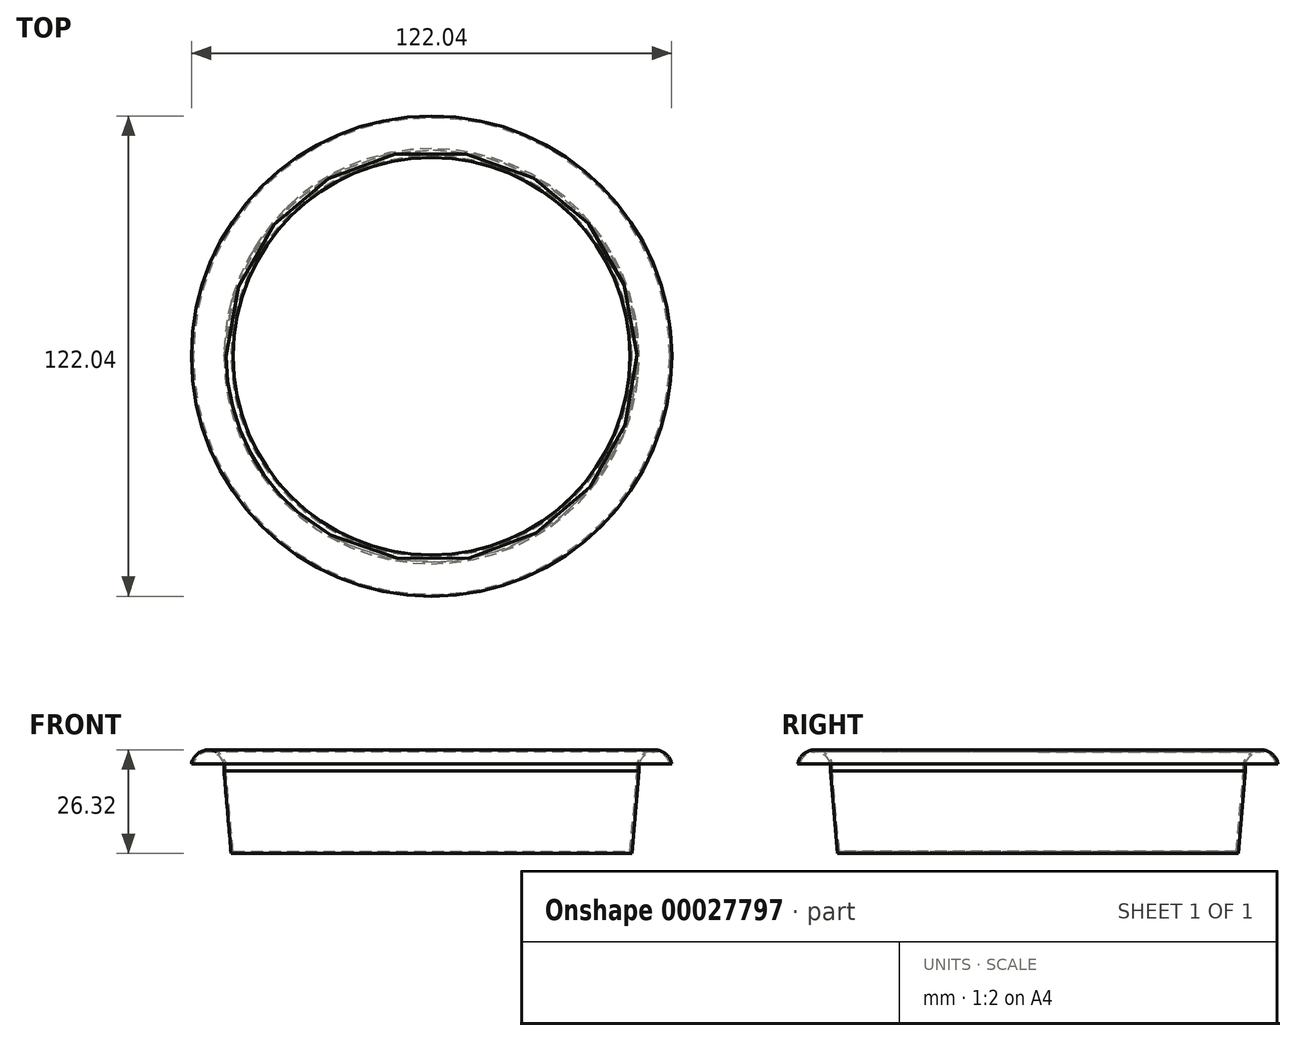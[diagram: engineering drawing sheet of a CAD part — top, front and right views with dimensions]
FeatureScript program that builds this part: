
annotation { "Feature Type Name" : "Feature", "Feature Type Description" : "" }
export const myFeature = defineFeature(function(context is Context, id is Id, definition is map)
    precondition{}
    {
        {
            var Q0;
            Q0=qCreatedBy(makeId("Front.planeOp"),FACE);
            var sketch = newSketch(context, id + "F0", { "sketchPlane" : qUnion([Q0])});
            skLineSegment(sketch, "E0", {"start": v(0, 0) * mm, "end": v(-50.92, 0) * mm});
            skLineSegment(sketch, "E1", {"start": v(-50.92, 0) * mm, "end": v(-52.74, 21.02) * mm});
            skArc(sketch, "E2", {"start": v(-52.74, 21.02) * mm, "mid": v(-55.8, 25.72) * mm, "end": v(-60.53, 22.7) * mm});
            skArc(sketch, "E3.0", {"start": v(-52.23, 21) * mm, "mid": v(-55.74, 26.23) * mm, "end": v(-61.02, 22.8) * mm});
            skLineSegment(sketch, "E3.1", {"start": v(-50.46, 0.5) * mm, "end": v(-52.23, 21) * mm});
            skLineSegment(sketch, "E3.2", {"start": v(0, 0.5) * mm, "end": v(-50.46, 0.5) * mm});
            skLineSegment(sketch, "E4", {"start": v(-60.53, 22.7) * mm, "end": v(-61.02, 22.8) * mm});
            skLineSegment(sketch, "E5", {"start": v(0, 0) * mm, "end": v(0, 0.5) * mm});
            skLineSegment(sketch, "E6", {"start": v(0, 0.5) * mm, "end": v(0, 36.82) * mm});
            skSolve(sketch);
        }
        {
            var Q0;
            Q0 = qSketchRegion(id + "F0", true);
            var Q1;
            Q1=sQuery(id+"F0.wireOp",EDGE,"E6");
            revolve(context, id + "F1", {"entities" : qUnion([Q0]), "axis" : qUnion([Q1]), "revolveType" : RevolveType.FULL});
        }
    });
